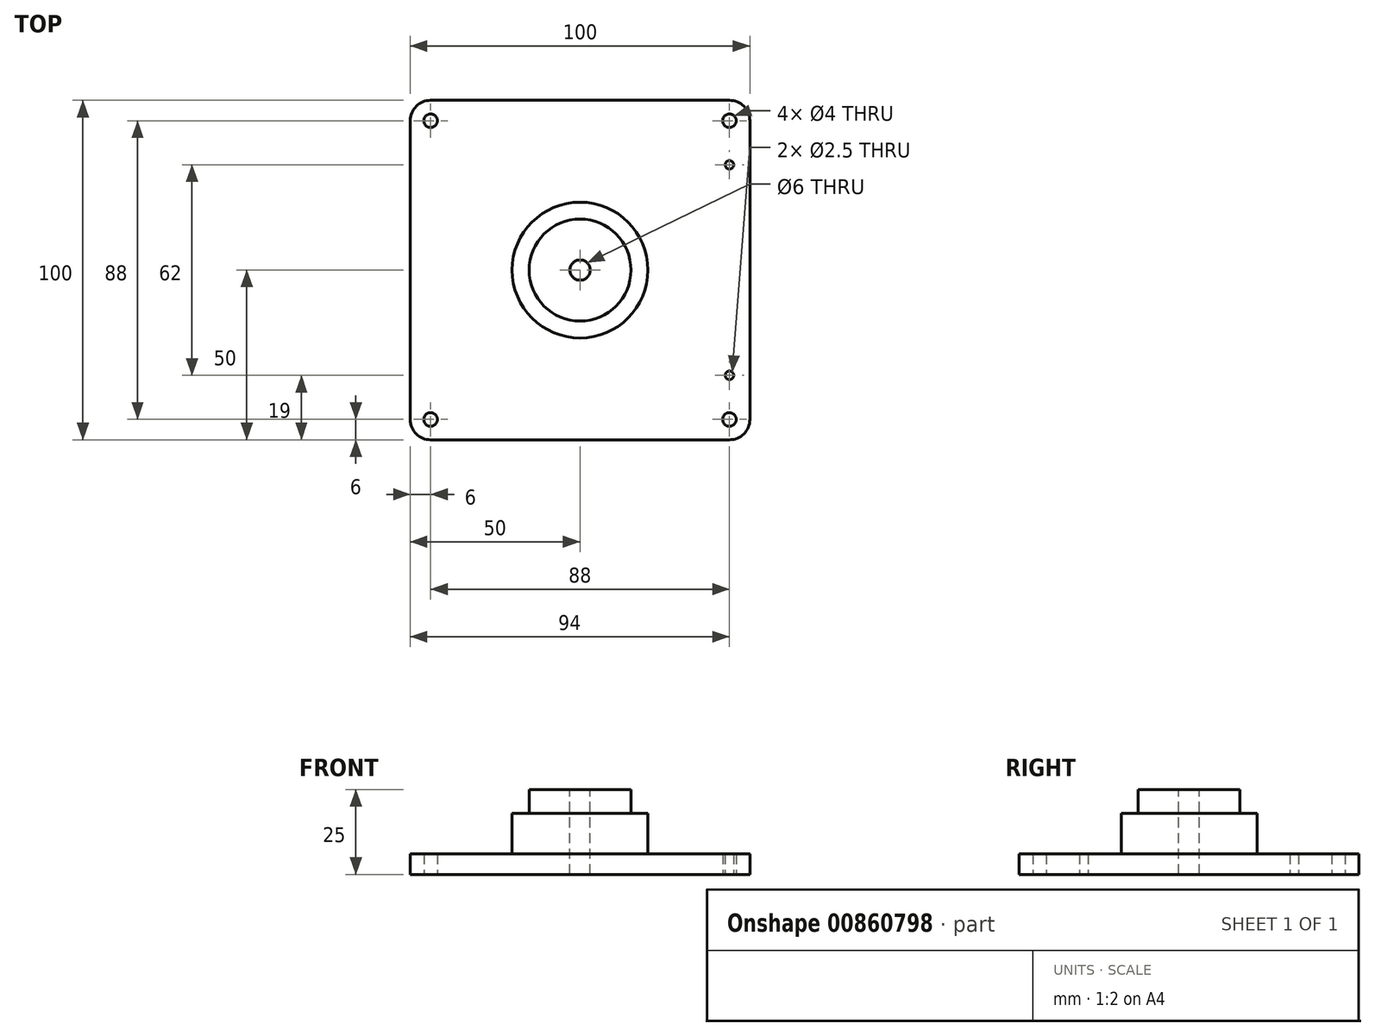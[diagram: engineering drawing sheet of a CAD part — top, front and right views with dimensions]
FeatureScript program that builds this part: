
annotation { "Feature Type Name" : "Feature", "Feature Type Description" : "" }
export const myFeature = defineFeature(function(context is Context, id is Id, definition is map)
    precondition{}
    {
        {
            var Q0;
            Q0=qCreatedBy(makeId("Top.planeOp"),FACE);
            var sketch = newSketch(context, id + "F0", { "sketchPlane" : qUnion([Q0])});
            skLineSegment(sketch, "E0.bottom", {"start": v(6, 0) * mm, "end": v(94, 0) * mm});
            skLineSegment(sketch, "E0.top", {"start": v(6, 100) * mm, "end": v(25, 100) * mm});
            skLineSegment(sketch, "E0.left", {"start": v(0, 6) * mm, "end": v(0, 94) * mm});
            skLineSegment(sketch, "E0.right", {"start": v(100, 6) * mm, "end": v(100, 94) * mm});
            skPoint(sketch, "E1.visualSharp", {"position": v(0, 0) * mm});
            skArc(sketch, "E1.filletArc", {"start": v(0, 6) * mm, "mid": v(1.76, 1.76) * mm, "end": v(6, 0) * mm});
            skPoint(sketch, "E2.visualSharp", {"position": v(100, 0) * mm});
            skArc(sketch, "E2.filletArc", {"start": v(94, 0) * mm, "mid": v(98.24, 1.76) * mm, "end": v(100, 6) * mm});
            skPoint(sketch, "E3.visualSharp", {"position": v(0, 100) * mm});
            skArc(sketch, "E3.filletArc", {"start": v(6, 100) * mm, "mid": v(1.76, 98.24) * mm, "end": v(0, 94) * mm});
            skPoint(sketch, "E4.visualSharp", {"position": v(100, 100) * mm});
            skArc(sketch, "E4.filletArc", {"start": v(100, 94) * mm, "mid": v(98.24, 98.24) * mm, "end": v(94, 100) * mm});
            skLineSegment(sketch, "E5.top", {"start": v(25, 136) * mm, "end": v(75, 136) * mm});
            skLineSegment(sketch, "E5.left", {"start": v(25, 100) * mm, "end": v(25, 136) * mm});
            skLineSegment(sketch, "E5.right", {"start": v(75, 100) * mm, "end": v(75, 136) * mm});
            skLineSegment(sketch, "E6.trimOffspring", {"start": v(75, 100) * mm, "end": v(94, 100) * mm});
            skCircle(sketch, "E7", {"center": v(50, 99.5) * mm, "radius": 10 * mm});
            skPoint(sketch, "E7.centerSnap0", {"position": v(50, 136) * mm});
            skPoint(sketch, "E8", {"position": v(50, 50) * mm});
            skPoint(sketch, "E8.positionSnap0", {"position": v(50, 0) * mm});
            skPoint(sketch, "E8.positionSnap1", {"position": v(0, 50) * mm});
            skLineSegment(sketch, "E9.left", {"start": v(33, 112) * mm, "end": v(33, 118) * mm});
            skLineSegment(sketch, "E9.right", {"start": v(36, 112) * mm, "end": v(36, 118) * mm});
            skLineSegment(sketch, "E10", {"start": v(50, 99.5) * mm, "end": v(50, 123) * mm, "construction": true});
            skLineSegment(sketch, "E11", {"start": v(50, 99.5) * mm, "end": v(33.46, 99.5) * mm, "construction": true});
            skArc(sketch, "E12", {"start": v(36, 118) * mm, "mid": v(34.5, 119.5) * mm, "end": v(33, 118) * mm});
            skArc(sketch, "E13", {"start": v(33, 112) * mm, "mid": v(34.5, 110.5) * mm, "end": v(36, 112) * mm});
            skLineSegment(sketch, "E14.MirrorCS", {"start": v(64, 112) * mm, "end": v(64, 118) * mm});
            skArc(sketch, "E15.MirrorCS", {"start": v(64, 118) * mm, "mid": v(65.5, 119.5) * mm, "end": v(67, 118) * mm});
            skLineSegment(sketch, "E16.MirrorCS", {"start": v(67, 112) * mm, "end": v(67, 118) * mm});
            skArc(sketch, "E17.MirrorCS", {"start": v(67, 112) * mm, "mid": v(65.5, 110.5) * mm, "end": v(64, 112) * mm});
            skArc(sketch, "E18.MirrorCS", {"start": v(33, 87) * mm, "mid": v(34.5, 88.5) * mm, "end": v(36, 87) * mm});
            skLineSegment(sketch, "E19.MirrorCS", {"start": v(33, 87) * mm, "end": v(33, 81) * mm});
            skLineSegment(sketch, "E20.MirrorCS", {"start": v(36, 87) * mm, "end": v(36, 81) * mm});
            skArc(sketch, "E21.MirrorCS", {"start": v(36, 81) * mm, "mid": v(34.5, 79.5) * mm, "end": v(33, 81) * mm});
            skLineSegment(sketch, "E22.MirrorCS", {"start": v(64, 87) * mm, "end": v(64, 81) * mm});
            skArc(sketch, "E23.MirrorCS", {"start": v(64, 81) * mm, "mid": v(65.5, 79.5) * mm, "end": v(67, 81) * mm});
            skLineSegment(sketch, "E24.MirrorCS", {"start": v(67, 87) * mm, "end": v(67, 81) * mm});
            skArc(sketch, "E25.MirrorCS", {"start": v(67, 87) * mm, "mid": v(65.5, 88.5) * mm, "end": v(64, 87) * mm});
            skCircle(sketch, "E26", {"center": v(94, 94) * mm, "radius": 2 * mm});
            skCircle(sketch, "E27", {"center": v(6, 94) * mm, "radius": 2 * mm});
            skCircle(sketch, "E28", {"center": v(94, 6) * mm, "radius": 2 * mm});
            skCircle(sketch, "E29", {"center": v(6, 6) * mm, "radius": 2 * mm});
            skCircle(sketch, "E30", {"center": v(94, 81) * mm, "radius": 1.25 * mm});
            skCircle(sketch, "E31", {"center": v(94, 19) * mm, "radius": 1.25 * mm});
            skSolve(sketch);
        }
        {
            var Q0;
            Q0=makeQuery(id+"F0.imprint","IMPRINT",FACE,{"disambiguationData":[TD([[makeQuery(id+"F0.imprint","IMPRINT",EDGE,{"derivedFrom":sQuery(id+"F0.wireOp",EDGE,"E0.bottom")}),1.0]])]});
            extrude(context, id + "F1", {"entities" : qUnion([Q0]), "depth" : 6 * mm, "offsetDistance" : 25 * mm});
        }
        {
            var Q0;
            Q0=makeQuery(id+"F1.opExtrude","CAP_FACE",FACE,{"disambiguationData":[OSD([sQuery(id+"F0.wireOp",EDGE,"E0.bottom"),sQuery(id+"F0.wireOp",EDGE,"E0.top"),sQuery(id+"F0.wireOp",EDGE,"E0.left"),sQuery(id+"F0.wireOp",EDGE,"E0.right"),sQuery(id+"F0.wireOp",EDGE,"E1.filletArc"),sQuery(id+"F0.wireOp",EDGE,"E2.filletArc"),sQuery(id+"F0.wireOp",EDGE,"E3.filletArc"),sQuery(id+"F0.wireOp",EDGE,"E4.filletArc"),sQuery(id+"F0.wireOp",EDGE,"E5.top"),sQuery(id+"F0.wireOp",EDGE,"E5.left"),sQuery(id+"F0.wireOp",EDGE,"E5.right"),sQuery(id+"F0.wireOp",EDGE,"E6.trimOffspring"),sQuery(id+"F0.wireOp",EDGE,"E7"),sQuery(id+"F0.wireOp",EDGE,"E9.left"),sQuery(id+"F0.wireOp",EDGE,"E9.right"),sQuery(id+"F0.wireOp",EDGE,"E12"),sQuery(id+"F0.wireOp",EDGE,"E13"),sQuery(id+"F0.wireOp",EDGE,"E14.MirrorCS"),sQuery(id+"F0.wireOp",EDGE,"E15.MirrorCS"),sQuery(id+"F0.wireOp",EDGE,"E16.MirrorCS"),sQuery(id+"F0.wireOp",EDGE,"E17.MirrorCS"),sQuery(id+"F0.wireOp",EDGE,"E18.MirrorCS"),sQuery(id+"F0.wireOp",EDGE,"E19.MirrorCS"),sQuery(id+"F0.wireOp",EDGE,"E20.MirrorCS"),sQuery(id+"F0.wireOp",EDGE,"E21.MirrorCS"),sQuery(id+"F0.wireOp",EDGE,"E22.MirrorCS"),sQuery(id+"F0.wireOp",EDGE,"E23.MirrorCS"),sQuery(id+"F0.wireOp",EDGE,"E24.MirrorCS"),sQuery(id+"F0.wireOp",EDGE,"E25.MirrorCS"),sQuery(id+"F0.wireOp",EDGE,"E26"),sQuery(id+"F0.wireOp",EDGE,"E27"),sQuery(id+"F0.wireOp",EDGE,"E28"),sQuery(id+"F0.wireOp",EDGE,"E29"),sQuery(id+"F0.wireOp",EDGE,"E30"),sQuery(id+"F0.wireOp",EDGE,"E31")])],"isStart":false});
            var sketch = newSketch(context, id + "F2", { "sketchPlane" : qUnion([Q0])});
            skCircle(sketch, "E32", {"center": v(50, 50) * mm, "radius": 20 * mm});
            skPoint(sketch, "E32.centerSnap0", {"position": v(50, 0) * mm});
            skPoint(sketch, "E32.centerSnap1", {"position": v(0, 50) * mm});
            skSolve(sketch);
        }
        {
            var Q0;
            Q0=qSketchRegion(id+"F2",true);
            extrude(context, id + "F3", {"entities" : qUnion([Q0]), "operationType" : NewBodyOperationType.ADD, "depth" : 12 * mm, "offsetDistance" : 25 * mm});
        }
        {
            var Q0;
            Q0=makeQuery(id+"F3.opExtrude","CAP_FACE",FACE,{"disambiguationData":[OSD([sQuery(id+"F2.wireOp",EDGE,"E32")])],"isStart":false});
            var sketch = newSketch(context, id + "F4", { "sketchPlane" : qUnion([Q0])});
            skCircle(sketch, "E33", {"center": v(50, 50) * mm, "radius": 15 * mm});
            skSolve(sketch);
        }
        {
            var Q0;
            Q0=qSketchRegion(id+"F4",true);
            extrude(context, id + "F5", {"entities" : qUnion([Q0]), "operationType" : NewBodyOperationType.ADD, "depth" : 7 * mm, "offsetDistance" : 25 * mm});
        }
        {
            var Q0;
            Q0=makeQuery(id+"F5.opExtrude","CAP_FACE",FACE,{"disambiguationData":[OSD([sQuery(id+"F4.wireOp",EDGE,"E33")])],"isStart":false});
            var sketch = newSketch(context, id + "F6", { "sketchPlane" : qUnion([Q0])});
            skCircle(sketch, "E34", {"center": v(50, 50) * mm, "radius": 3 * mm});
            skSolve(sketch);
        }
        {
            var Q0;
            Q0=qSketchRegion(id+"F6",true);
            extrude(context, id + "F7", {"entities" : qUnion([Q0]), "operationType" : NewBodyOperationType.REMOVE, "endBound" : BoundingType.THROUGH_ALL, "oppositeDirection" : true, "depth" : 25 * mm, "offsetDistance" : 25 * mm});
        }
        {
            var Q0;
            Q0=makeQuery(id+"F1.opExtrude","CAP_FACE",FACE,{"disambiguationData":[OSD([sQuery(id+"F0.wireOp",EDGE,"E0.bottom"),sQuery(id+"F0.wireOp",EDGE,"E0.top"),sQuery(id+"F0.wireOp",EDGE,"E0.left"),sQuery(id+"F0.wireOp",EDGE,"E0.right"),sQuery(id+"F0.wireOp",EDGE,"E1.filletArc"),sQuery(id+"F0.wireOp",EDGE,"E2.filletArc"),sQuery(id+"F0.wireOp",EDGE,"E3.filletArc"),sQuery(id+"F0.wireOp",EDGE,"E4.filletArc"),sQuery(id+"F0.wireOp",EDGE,"E5.top"),sQuery(id+"F0.wireOp",EDGE,"E5.left"),sQuery(id+"F0.wireOp",EDGE,"E5.right"),sQuery(id+"F0.wireOp",EDGE,"E6.trimOffspring"),sQuery(id+"F0.wireOp",EDGE,"E7"),sQuery(id+"F0.wireOp",EDGE,"E9.left"),sQuery(id+"F0.wireOp",EDGE,"E9.right"),sQuery(id+"F0.wireOp",EDGE,"E12"),sQuery(id+"F0.wireOp",EDGE,"E13"),sQuery(id+"F0.wireOp",EDGE,"E14.MirrorCS"),sQuery(id+"F0.wireOp",EDGE,"E15.MirrorCS"),sQuery(id+"F0.wireOp",EDGE,"E16.MirrorCS"),sQuery(id+"F0.wireOp",EDGE,"E17.MirrorCS"),sQuery(id+"F0.wireOp",EDGE,"E18.MirrorCS"),sQuery(id+"F0.wireOp",EDGE,"E19.MirrorCS"),sQuery(id+"F0.wireOp",EDGE,"E20.MirrorCS"),sQuery(id+"F0.wireOp",EDGE,"E21.MirrorCS"),sQuery(id+"F0.wireOp",EDGE,"E22.MirrorCS"),sQuery(id+"F0.wireOp",EDGE,"E23.MirrorCS"),sQuery(id+"F0.wireOp",EDGE,"E24.MirrorCS"),sQuery(id+"F0.wireOp",EDGE,"E25.MirrorCS"),sQuery(id+"F0.wireOp",EDGE,"E26"),sQuery(id+"F0.wireOp",EDGE,"E27"),sQuery(id+"F0.wireOp",EDGE,"E28"),sQuery(id+"F0.wireOp",EDGE,"E29"),sQuery(id+"F0.wireOp",EDGE,"E30"),sQuery(id+"F0.wireOp",EDGE,"E31")])],"isStart":false});
            var sketch = newSketch(context, id + "F8", { "sketchPlane" : qUnion([Q0])});
            skLineSegment(sketch, "E35.bottom", {"start": v(4.23, 144.4) * mm, "end": v(84.5, 144.4) * mm});
            skLineSegment(sketch, "E35.top", {"start": v(4.23, 100) * mm, "end": v(84.5, 100) * mm});
            skLineSegment(sketch, "E35.left", {"start": v(4.23, 144.4) * mm, "end": v(4.23, 100) * mm});
            skLineSegment(sketch, "E35.right", {"start": v(84.5, 144.4) * mm, "end": v(84.5, 100) * mm});
            skSolve(sketch);
        }
        {
            var Q0;
            Q0 = qSketchRegion(id + "F8", true);
            extrude(context, id + "F9", {"entities" : qUnion([Q0]), "operationType" : NewBodyOperationType.REMOVE, "oppositeDirection" : true, "depth" : 25 * mm, "offsetDistance" : 25 * mm});
        }
        {
            var Q0;
            Q0=makeQuery(id+"F1.opExtrude","CAP_FACE",FACE,{"disambiguationData":[OSD([sQuery(id+"F0.wireOp",EDGE,"E0.bottom"),sQuery(id+"F0.wireOp",EDGE,"E0.top"),sQuery(id+"F0.wireOp",EDGE,"E0.left"),sQuery(id+"F0.wireOp",EDGE,"E0.right"),sQuery(id+"F0.wireOp",EDGE,"E1.filletArc"),sQuery(id+"F0.wireOp",EDGE,"E2.filletArc"),sQuery(id+"F0.wireOp",EDGE,"E3.filletArc"),sQuery(id+"F0.wireOp",EDGE,"E4.filletArc"),sQuery(id+"F0.wireOp",EDGE,"E5.top"),sQuery(id+"F0.wireOp",EDGE,"E5.left"),sQuery(id+"F0.wireOp",EDGE,"E5.right"),sQuery(id+"F0.wireOp",EDGE,"E6.trimOffspring"),sQuery(id+"F0.wireOp",EDGE,"E7"),sQuery(id+"F0.wireOp",EDGE,"E9.left"),sQuery(id+"F0.wireOp",EDGE,"E9.right"),sQuery(id+"F0.wireOp",EDGE,"E12"),sQuery(id+"F0.wireOp",EDGE,"E13"),sQuery(id+"F0.wireOp",EDGE,"E14.MirrorCS"),sQuery(id+"F0.wireOp",EDGE,"E15.MirrorCS"),sQuery(id+"F0.wireOp",EDGE,"E16.MirrorCS"),sQuery(id+"F0.wireOp",EDGE,"E17.MirrorCS"),sQuery(id+"F0.wireOp",EDGE,"E18.MirrorCS"),sQuery(id+"F0.wireOp",EDGE,"E19.MirrorCS"),sQuery(id+"F0.wireOp",EDGE,"E20.MirrorCS"),sQuery(id+"F0.wireOp",EDGE,"E21.MirrorCS"),sQuery(id+"F0.wireOp",EDGE,"E22.MirrorCS"),sQuery(id+"F0.wireOp",EDGE,"E23.MirrorCS"),sQuery(id+"F0.wireOp",EDGE,"E24.MirrorCS"),sQuery(id+"F0.wireOp",EDGE,"E25.MirrorCS"),sQuery(id+"F0.wireOp",EDGE,"E26"),sQuery(id+"F0.wireOp",EDGE,"E27"),sQuery(id+"F0.wireOp",EDGE,"E28"),sQuery(id+"F0.wireOp",EDGE,"E29"),sQuery(id+"F0.wireOp",EDGE,"E30"),sQuery(id+"F0.wireOp",EDGE,"E31")])],"isStart":false});
            var sketch = newSketch(context, id + "F10", { "sketchPlane" : qUnion([Q0])});
            skLineSegment(sketch, "E36.bottom", {"start": v(18.71, 100) * mm, "end": v(78.55, 100) * mm});
            skLineSegment(sketch, "E36.top", {"start": v(18.71, 77.25) * mm, "end": v(78.55, 77.25) * mm});
            skLineSegment(sketch, "E36.left", {"start": v(18.71, 100) * mm, "end": v(18.71, 77.25) * mm});
            skLineSegment(sketch, "E36.right", {"start": v(78.55, 100) * mm, "end": v(78.55, 77.25) * mm});
            skSolve(sketch);
        }
        {
            var Q0;
            Q0 = qSketchRegion(id + "F10", true);
            var Q1;
            Q1 = qConstructionFilter(qBodyType(qCreatedBy(id + "F10" ,EDGE), BodyType.WIRE), ConstructionObject.NO);
            extrude(context, id + "F11", {"entities" : qUnion([Q0]), "operationType" : NewBodyOperationType.ADD, "surfaceOperationType" : NewSurfaceOperationType.ADD, "surfaceEntities" : qUnion([Q1]), "oppositeDirection" : true, "depth" : 6 * mm, "offsetDistance" : 25 * mm});
        }
    });
